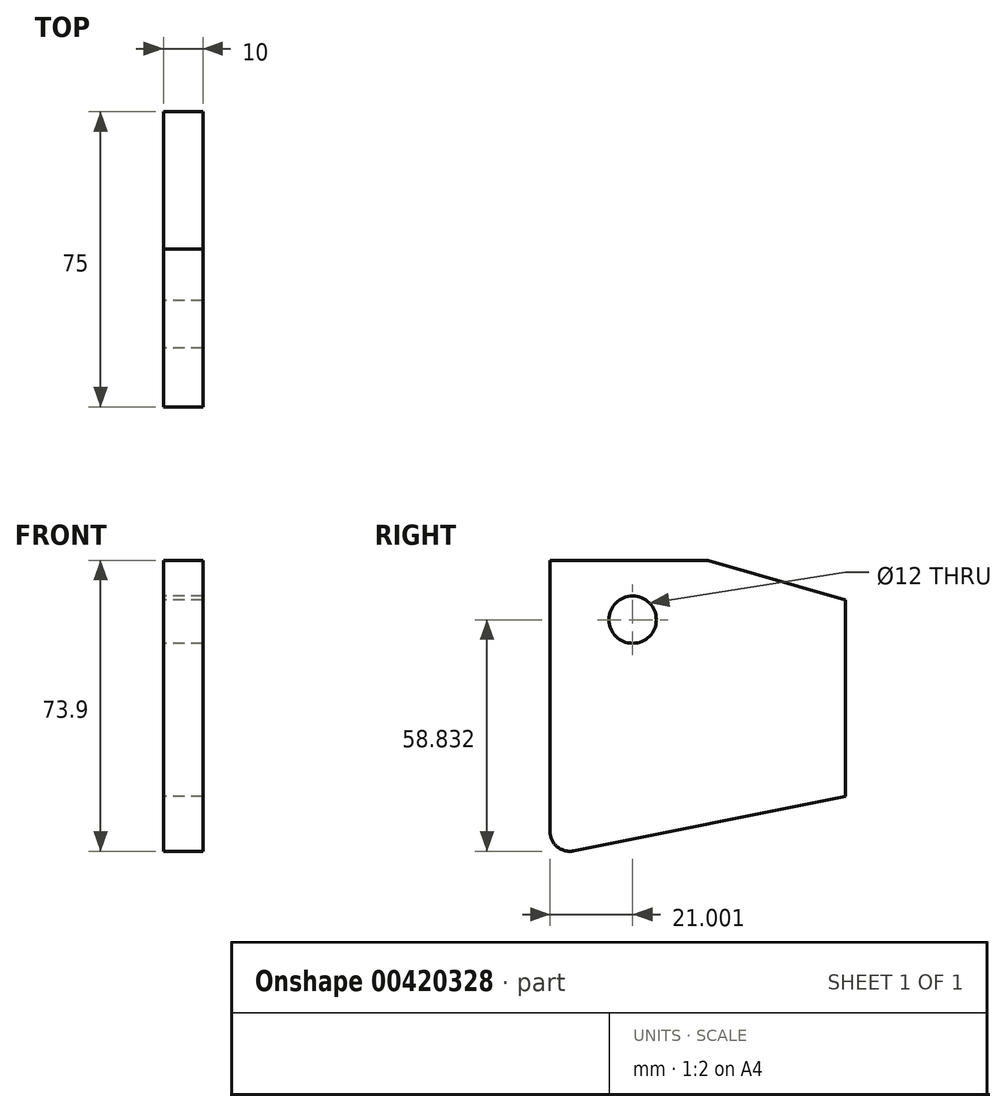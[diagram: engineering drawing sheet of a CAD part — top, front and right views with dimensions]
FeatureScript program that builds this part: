
annotation { "Feature Type Name" : "Feature", "Feature Type Description" : "" }
export const myFeature = defineFeature(function(context is Context, id is Id, definition is map)
    precondition{}
    {
        {
            var Q0;
            Q0=qCreatedBy(makeId("Right.planeOp"),FACE);
            var sketch = newSketch(context, id + "F0", { "sketchPlane" : qUnion([Q0])});
            skLineSegment(sketch, "E0.top", {"start": v(82.98, -26.14) * mm, "end": v(7.98, -26.14) * mm});
            skLineSegment(sketch, "E0.right", {"start": v(7.98, 33.86) * mm, "end": v(7.98, -26.14) * mm});
            skLineSegment(sketch, "E1", {"start": v(82.98, -26.14) * mm, "end": v(82.98, 23.86) * mm});
            skLineSegment(sketch, "E2", {"start": v(82.98, 23.86) * mm, "end": v(48.14, 33.86) * mm});
            skLineSegment(sketch, "E3", {"start": v(48.14, 33.86) * mm, "end": v(7.98, 33.86) * mm});
            skLineSegment(sketch, "E4.bottom", {"start": v(7.98, -26.14) * mm, "end": v(82.98, -26.14) * mm});
            skLineSegment(sketch, "E5", {"start": v(7.98, -26.14) * mm, "end": v(7.98, -41.14) * mm});
            skLineSegment(sketch, "E6", {"start": v(7.98, -41.14) * mm, "end": v(82.98, -26.14) * mm});
            skSolve(sketch);
        }
        {
            var Q0;
            Q0=qSketchRegion(id+"F0",true);
            extrude(context, id + "F1", {"entities" : qUnion([Q0]), "depth" : 10 * mm});
        }
        {
            var Q0;
            Q0=makeQuery(id+"F1.opExtrude","CAP_FACE",FACE,{"disambiguationData":[OSD([sQuery(id+"F0.wireOp",EDGE,"E0.bottom"),sQuery(id+"F0.wireOp",EDGE,"E0.top"),sQuery(id+"F0.wireOp",EDGE,"E0.left"),sQuery(id+"F0.wireOp",EDGE,"E0.right")])],"isStart":true});
            var sketch = newSketch(context, id + "F2", { "sketchPlane" : qUnion([Q0])});
            skCircle(sketch, "E7", {"center": v(-28.98, 18.8) * mm, "radius": 6 * mm});
            skLineSegment(sketch, "E8", {"start": v(-28.98, 18.8) * mm, "end": v(-28.98, -31.2) * mm, "construction": true});
            skSolve(sketch);
        }
        {
            var Q0;
            Q0=qSketchRegion(id+"F2",true);
            extrude(context, id + "F3", {"entities" : qUnion([Q0]), "operationType" : NewBodyOperationType.REMOVE, "endBound" : BoundingType.THROUGH_ALL, "oppositeDirection" : true, "depth" : 25 * mm});
        }
        {
            var Q0;
            Q0=makeQuery(id+"F1.opExtrude","SWEPT_EDGE",EDGE,{"disambiguationData":[OSD([sQuery(id+"F0.wireOp",EDGE,"E5"),sQuery(id+"F0.wireOp",EDGE,"E6")])]});
            fillet(context, id + "F4", {"entities" : qUnion([Q0]), "radius" : 5 * mm, "tangentPropagation" : true, "allowEdgeOverflow" : false});
        }
    });
